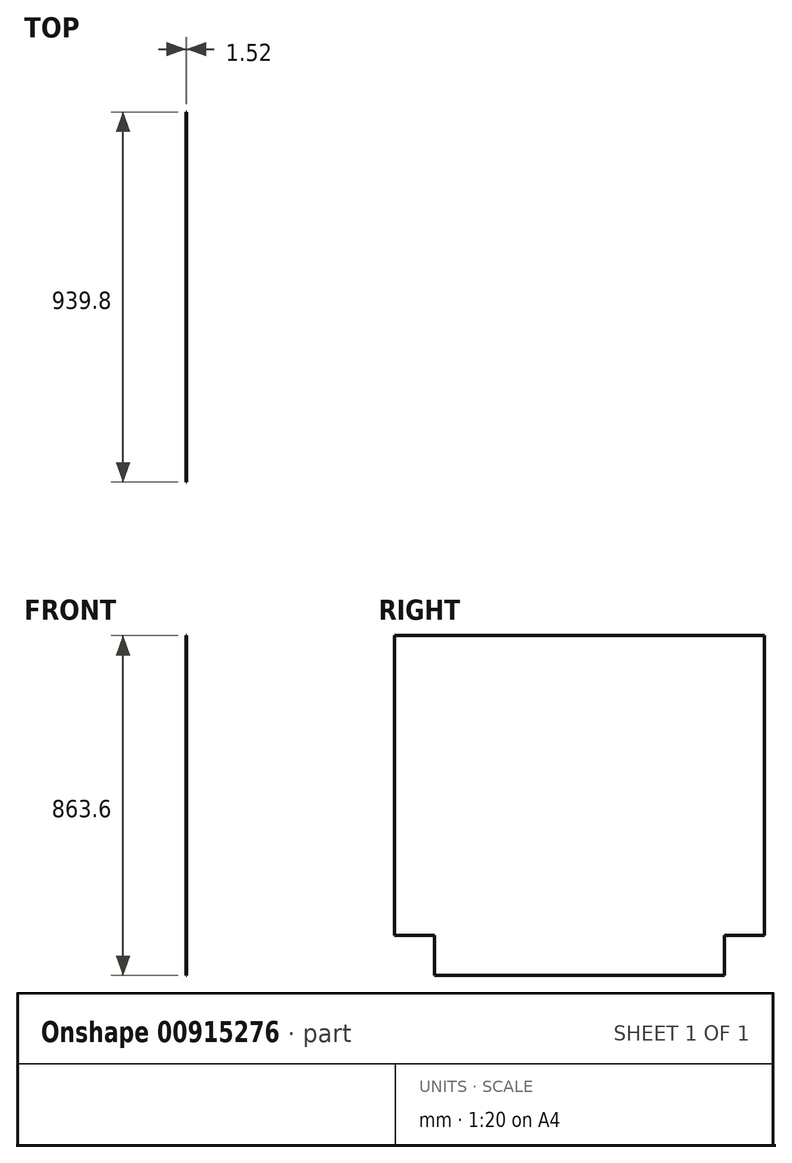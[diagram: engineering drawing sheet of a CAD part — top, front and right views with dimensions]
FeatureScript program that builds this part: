
annotation { "Feature Type Name" : "Feature", "Feature Type Description" : "" }
export const myFeature = defineFeature(function(context is Context, id is Id, definition is map)
    precondition{}
    {
        {
            var Q0;
            Q0=qCreatedBy(makeId("Right.planeOp"),FACE);
            var sketch = newSketch(context, id + "F0", { "sketchPlane" : qUnion([Q0])});
            skLineSegment(sketch, "E0.bottom", {"start": v(-469.9, 431.8) * mm, "end": v(469.9, 431.8) * mm});
            skLineSegment(sketch, "E0.top", {"start": v(-469.9, -431.8) * mm, "end": v(469.9, -431.8) * mm});
            skLineSegment(sketch, "E0.left", {"start": v(-469.9, 431.8) * mm, "end": v(-469.9, -431.8) * mm});
            skLineSegment(sketch, "E0.right", {"start": v(469.9, 431.8) * mm, "end": v(469.9, -431.8) * mm});
            skPoint(sketch, "E0.middle", {"position": v(0, 0) * mm});
            skLineSegment(sketch, "E1.bottom", {"start": v(469.9, -431.8) * mm, "end": v(368.3, -431.8) * mm});
            skLineSegment(sketch, "E1.top", {"start": v(469.9, -330.2) * mm, "end": v(368.3, -330.2) * mm});
            skLineSegment(sketch, "E1.left", {"start": v(469.9, -431.8) * mm, "end": v(469.9, -330.2) * mm});
            skLineSegment(sketch, "E1.right", {"start": v(368.3, -431.8) * mm, "end": v(368.3, -330.2) * mm});
            skLineSegment(sketch, "E2.bottom", {"start": v(-469.9, -431.8) * mm, "end": v(-368.3, -431.8) * mm});
            skLineSegment(sketch, "E2.top", {"start": v(-469.9, -330.2) * mm, "end": v(-368.3, -330.2) * mm});
            skLineSegment(sketch, "E2.left", {"start": v(-469.9, -431.8) * mm, "end": v(-469.9, -330.2) * mm});
            skLineSegment(sketch, "E2.right", {"start": v(-368.3, -431.8) * mm, "end": v(-368.3, -330.2) * mm});
            skSolve(sketch);
        }
        {
            var Q0;
            Q0=makeQuery(id+"F0.imprint","IMPRINT",FACE,{"disambiguationData":[TD([[makeQuery(id+"F0.imprint","IMPRINT",EDGE,{"derivedFrom":sQuery(id+"F0.wireOp",EDGE,"E0.bottom")}),-1.0]])]});
            extrude(context, id + "F1", {"entities" : qUnion([Q0]), "depth" : 1.52 * mm, "offsetDistance" : 25.4 * mm});
        }
    });
